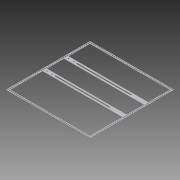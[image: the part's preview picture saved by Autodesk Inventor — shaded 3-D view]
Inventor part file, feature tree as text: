
AUTODESK INVENTOR PART (.ipt)
format: ipt  version: 2013 (Build 170138000, 138)  size: 9,533,440 bytes
history: native  units: in
note: dims shown in document units (in); Inventor stores cm internally (conversion verified against a paired STEP export)
features: reference x4, sketch x3, other x3, sheet_metal_op x2, extrude x1
ambient origin geometry x8: Origin, YZ Plane, XZ Plane, XY Plane, X Axis, Y Axis, Z Axis, Center Point
feature tree (13):
  extrude  "Extrusion2"  Depth=0.5in
  sheet_metal_op  "Face1"
  sketch  "Sketch2"  dims[d0=0.5in d3=0.5in]
  other  "Plate1"
  sheet_metal_op  "Bend1"
  sketch  "Sketch8"  dims[d4=0.5in]
  sketch  "Sketch9"  dims[d6=15.5in d7=14.1732in d9=0.4357in d10=0.3937in d12=1.0in d14=13.7795in d16=0.4357in d17=0.3937in d19=1.0in d21=19.25in d22=19.685in d24=0.3878in d25=0.3937in d27=1.0in d36=15.5in d42=0.4357in d43=0.25in d44=14.1732in d46=0.4357in d47=0.3937in d49=1.0in d51=18.5in d52=9.25in d53=0.125in d54=0.0in d55=1.0in d58=1.0in d59=5.0in d60=4.0in d61=0.125in d62=0.125in d63=0.0625in d64=0.25in d65=0.125in d96=0.266in d97=0.5in d98=3.5in d99=0.266in d100=0.5in d101=3.0in d102=0.266in d103=3.5in d104=0.5in d105=0.266in d106=0.5in d107=3.0in d108=0.125in d109=0.0in d110=0.125in d111=0.0in]
  reference  "Reference4"
  reference  "Reference5"
  reference  "Reference6"
  reference  "Reference7"
  other  "Cut6"
  other  "Cut7"
